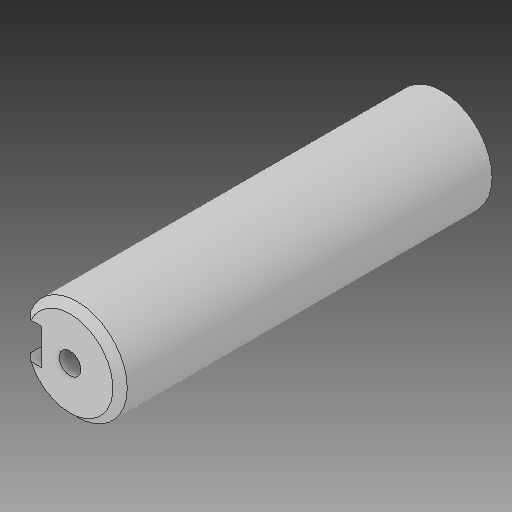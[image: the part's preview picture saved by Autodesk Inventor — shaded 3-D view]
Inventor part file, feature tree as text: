
AUTODESK INVENTOR PART (.ipt)
format: ipt  version: 2018 (Build 220112000, 112)  size: 116,736 bytes
history: native  units: mm
features: extrude x2, sketch x2, hole x1, plane x1, chamfer x1, projected_geometry x1
ambient origin geometry x8: Origin, YZ Plane, XZ Plane, XY Plane, X Axis, Y Axis, Z Axis, Center Point
bodies: Solid1 (feature_tree)
feature tree (8):
  extrude  "Extrusion1"  Depth=52.0mm TaperAngle=0.0deg
  hole  "Hole1"  [1 undecoded]
  plane  "Work Plane1"
  extrude  "Extrusion2"  TaperAngle=0.0deg  [1 undecoded]
  chamfer  "Chamfer1"  Distance=3.0mm
  sketch  "Sketch1"  dims[d0=14.0mm d1=52.0mm d2=0.0mm]
  sketch  "Sketch2"  dims[d3=10.0mm d4=10.0mm d5=3.0mm d6=6.0mm d7=4.0mm d8=2.0mm d9=90.0deg d10=13.0mm d11=0.0mm d12=5.0mm d14=0.0mm d17=3.0mm d18=0.0mm d19=1.0mm d20=2.0mm d21=45.0deg]
  projected_geometry  "Projected Loop1"
note: 2 required parameter values undecoded (feature->parameter linkage not recoverable at this tier; creation-order binding heuristic only, values carry confidence <= 0.55)
